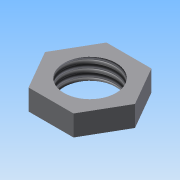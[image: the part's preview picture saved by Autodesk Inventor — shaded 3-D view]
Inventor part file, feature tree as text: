
AUTODESK INVENTOR PART (.ipt)
format: ipt  version: 2015 (Build 190159000, 159)  size: 84,992 bytes
history: native  units: mm
features: extrude x1, thread x1, sketch x1
ambient origin geometry x8: Origin, YZ Plane, XZ Plane, XY Plane, X Axis, Y Axis, Z Axis, Center Point
bodies: 实体1 (feature_tree)
feature tree (3):
  extrude  "拉伸1"  Depth=15.0mm
  thread  "螺纹1"  [1 undecoded]
  sketch  "草图1"  dims[d0=10.0mm d1=15.0mm d2=4.0mm d3=0.0mm d4=10.0mm d5=0.0mm]
note: 1 required parameter value undecoded (feature->parameter linkage not recoverable at this tier; creation-order binding heuristic only, values carry confidence <= 0.55)
